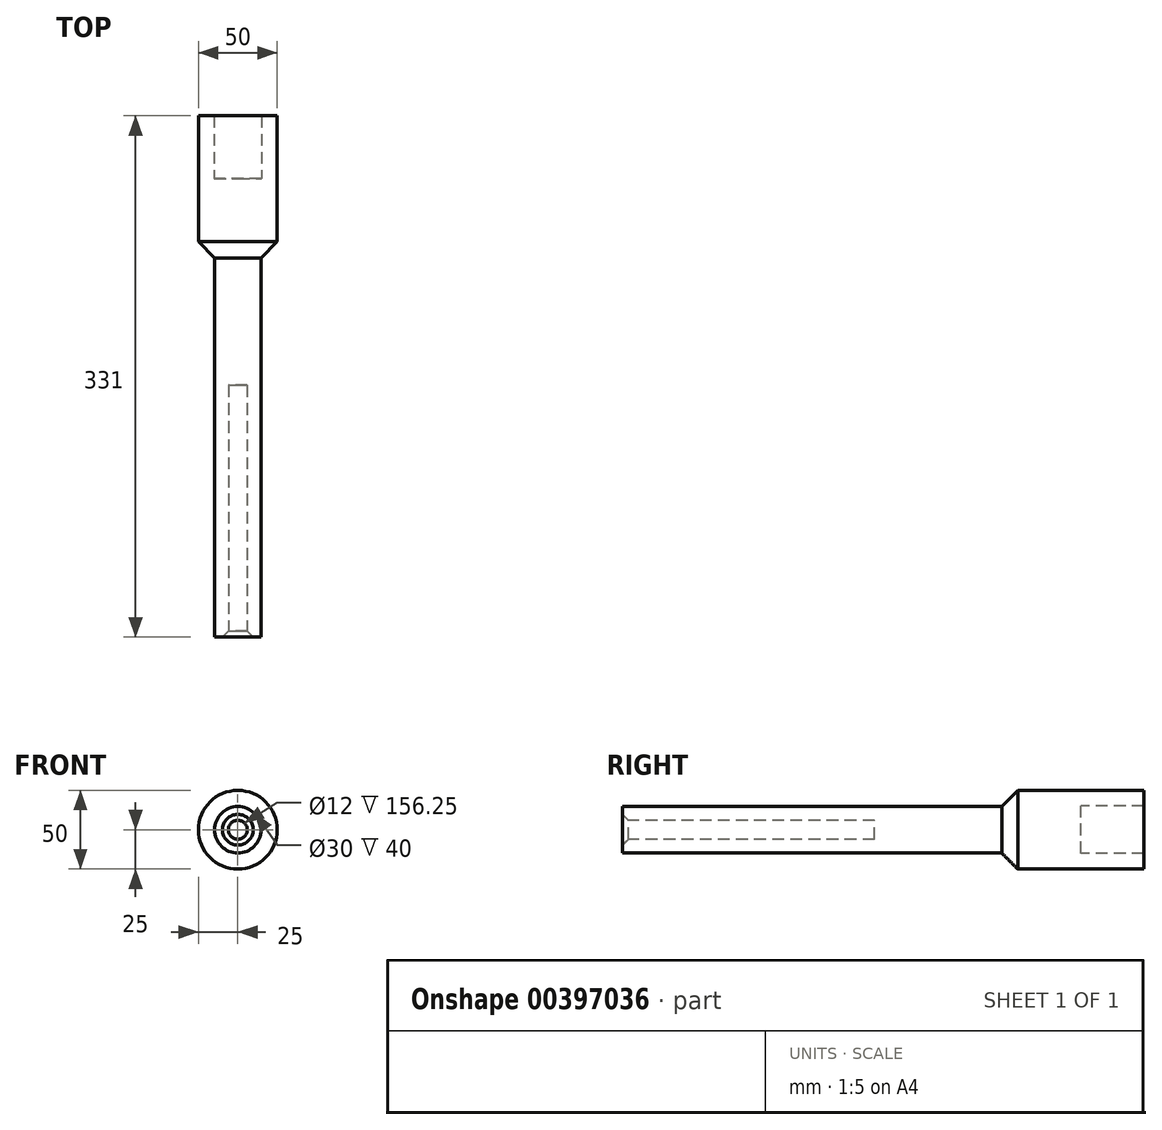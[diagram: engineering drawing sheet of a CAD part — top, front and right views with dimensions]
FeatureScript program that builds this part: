
annotation { "Feature Type Name" : "Feature", "Feature Type Description" : "" }
export const myFeature = defineFeature(function(context is Context, id is Id, definition is map)
    precondition{}
    {
        {
            var Q0;
            Q0=qCreatedBy(makeId("Right.planeOp"),FACE);
            var sketch = newSketch(context, id + "F0", { "sketchPlane" : qUnion([Q0])});
            skLineSegment(sketch, "E0", {"start": v(160, 0) * mm, "end": v(160, 6) * mm});
            skLineSegment(sketch, "E1", {"start": v(160, 6) * mm, "end": v(3.75, 6) * mm});
            skLineSegment(sketch, "E2", {"start": v(0, 9.75) * mm, "end": v(0, 14.75) * mm});
            skLineSegment(sketch, "E3", {"start": v(0, 14.75) * mm, "end": v(240.75, 14.75) * mm});
            skLineSegment(sketch, "E4", {"start": v(291, 25) * mm, "end": v(331, 25) * mm});
            skLineSegment(sketch, "E5", {"start": v(331, 25) * mm, "end": v(331, 15) * mm});
            skLineSegment(sketch, "E6", {"start": v(331, 15) * mm, "end": v(291, 15) * mm});
            skLineSegment(sketch, "E7", {"start": v(291, 15) * mm, "end": v(291, 0) * mm});
            skLineSegment(sketch, "E8", {"start": v(291, 0) * mm, "end": v(160, 0) * mm});
            skLineSegment(sketch, "E9", {"start": v(291, 15) * mm, "end": v(291, 25) * mm, "construction": true});
            skLineSegment(sketch, "E10", {"start": v(291, 25) * mm, "end": v(251, 25) * mm});
            skLineSegment(sketch, "E11", {"start": v(240.75, 14.75) * mm, "end": v(251, 25) * mm});
            skLineSegment(sketch, "E12", {"start": v(0, 0) * mm, "end": v(291, 0) * mm, "construction": true});
            skLineSegment(sketch, "E13", {"start": v(0, 9.75) * mm, "end": v(3.75, 6) * mm});
            skPoint(sketch, "E14.orphan", {"position": v(0, 6) * mm});
            skSolve(sketch);
        }
        {
            var Q0;
            Q0=makeQuery(id+"F0.imprint","IMPRINT",FACE,{"disambiguationData":[TD([[makeQuery(id+"F0.imprint","IMPRINT",EDGE,{"derivedFrom":sQuery(id+"F0.wireOp",EDGE,"E0")}),-1.0]])]});
            var Q1;
            Q1=sQuery(id+"F0.wireOp",EDGE,"E12");
            revolve(context, id + "F1", {"entities" : qUnion([Q0]), "axis" : qUnion([Q1]), "revolveType" : RevolveType.FULL});
        }
    });
